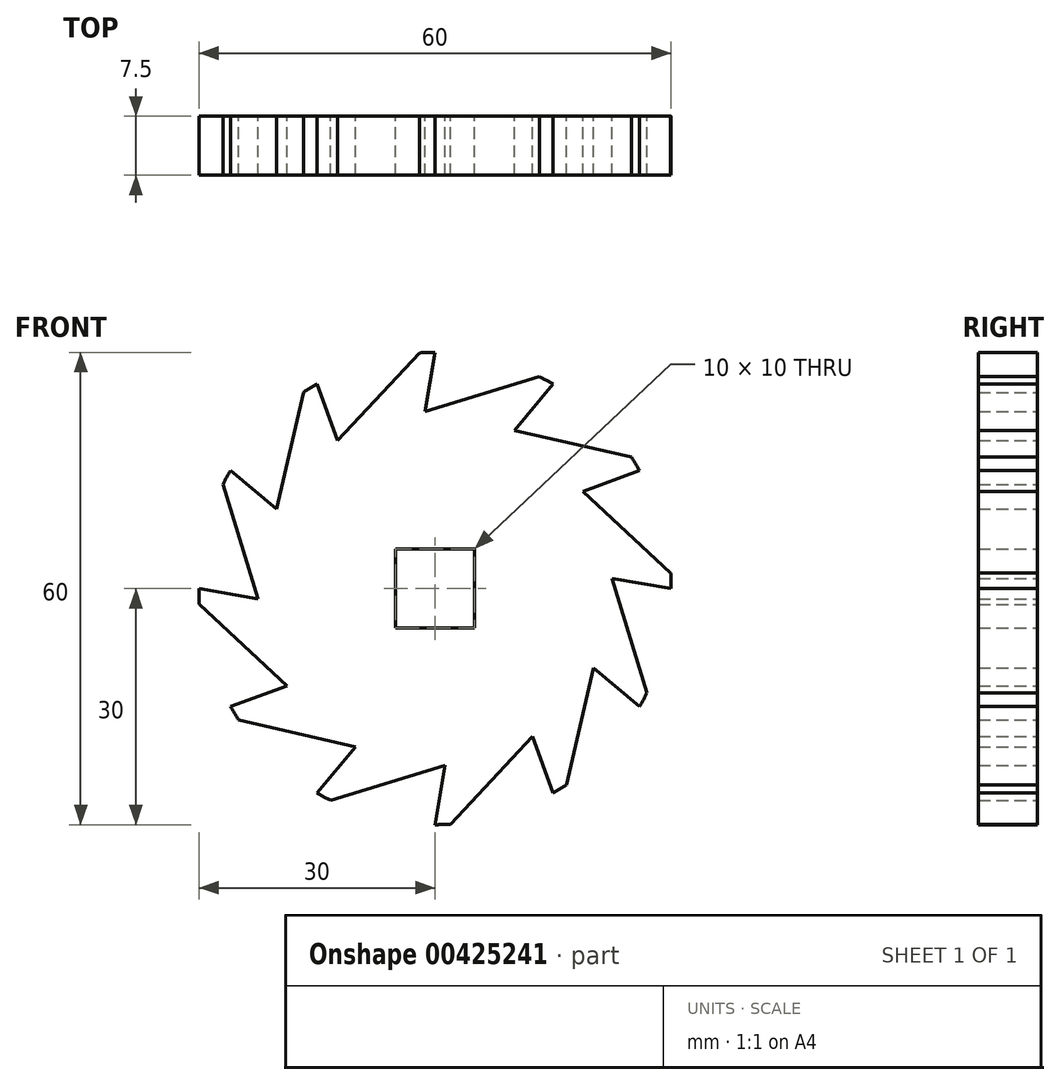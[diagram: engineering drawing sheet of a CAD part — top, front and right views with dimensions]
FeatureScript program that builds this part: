
annotation { "Feature Type Name" : "Feature", "Feature Type Description" : "" }
export const myFeature = defineFeature(function(context is Context, id is Id, definition is map)
    precondition{}
    {
        {
            var Q0;
            Q0=qCreatedBy(makeId("Front.planeOp"),FACE);
            var sketch = newSketch(context, id + "F0", { "sketchPlane" : qUnion([Q0])});
            skCircle(sketch, "E0", {"center": v(0, 0) * mm, "radius": 22.5 * mm, "construction": true});
            skLineSegment(sketch, "E1.bottom", {"start": v(5, 5) * mm, "end": v(-5, 5) * mm});
            skLineSegment(sketch, "E1.top", {"start": v(5, -5) * mm, "end": v(-5, -5) * mm});
            skLineSegment(sketch, "E1.left", {"start": v(5, 5) * mm, "end": v(5, -5) * mm});
            skLineSegment(sketch, "E1.right", {"start": v(-5, 5) * mm, "end": v(-5, -5) * mm});
            skCircle(sketch, "E2", {"center": v(0, 0) * mm, "radius": 30 * mm, "construction": true});
            skLineSegment(sketch, "E3", {"start": v(0, 0) * mm, "end": v(0, 30) * mm, "construction": true});
            skLineSegment(sketch, "E4", {"start": v(0, 0) * mm, "end": v(13.24, 26.92) * mm, "construction": true});
            skLineSegment(sketch, "E5", {"start": v(0, 30) * mm, "end": v(-1.3, 22.46) * mm, "construction": true});
            skLineSegment(sketch, "E6", {"start": v(-1.3, 22.46) * mm, "end": v(13.24, 26.92) * mm});
            skArc(sketch, "E7", {"start": v(13.24, 26.92) * mm, "mid": v(14.13, 26.46) * mm, "end": v(15, 25.98) * mm});
            skLineSegment(sketch, "E8", {"start": v(0, 0) * mm, "end": v(15, 25.98) * mm, "construction": true});
            skLineSegment(sketch, "E9.1.0", {"start": v(15, 25.98) * mm, "end": v(10.1, 20.1) * mm});
            skLineSegment(sketch, "E9.anchor1", {"start": v(0, 0) * mm, "end": v(-1.3, 22.46) * mm, "construction": true});
            skLineSegment(sketch, "E9.anchor2", {"start": v(0, 0) * mm, "end": v(10.1, 20.1) * mm, "construction": true});
            skLineSegment(sketch, "E10.1.0", {"start": v(-12.36, 18.8) * mm, "end": v(-2, 29.93) * mm});
            skArc(sketch, "E10.1.1", {"start": v(-2, 29.93) * mm, "mid": v(-1, 29.98) * mm, "end": v(0, 30) * mm});
            skLineSegment(sketch, "E10.1.2", {"start": v(0, 30) * mm, "end": v(-1.3, 22.46) * mm});
            skLineSegment(sketch, "E10.2.0", {"start": v(-20.1, 10.1) * mm, "end": v(-16.7, 24.93) * mm});
            skArc(sketch, "E10.2.1", {"start": v(-16.7, 24.93) * mm, "mid": v(-15.85, 25.47) * mm, "end": v(-15, 25.98) * mm});
            skLineSegment(sketch, "E10.2.2", {"start": v(-15, 25.98) * mm, "end": v(-12.36, 18.8) * mm});
            skLineSegment(sketch, "E10.3.0", {"start": v(-22.46, -1.3) * mm, "end": v(-26.92, 13.24) * mm});
            skArc(sketch, "E10.3.1", {"start": v(-26.92, 13.24) * mm, "mid": v(-26.46, 14.13) * mm, "end": v(-25.98, 15) * mm});
            skLineSegment(sketch, "E10.3.2", {"start": v(-25.98, 15) * mm, "end": v(-20.1, 10.1) * mm});
            skLineSegment(sketch, "E10.4.0", {"start": v(-18.8, -12.36) * mm, "end": v(-29.93, -2) * mm});
            skArc(sketch, "E10.4.1", {"start": v(-29.93, -2) * mm, "mid": v(-29.98, -1) * mm, "end": v(-30, 0) * mm});
            skLineSegment(sketch, "E10.4.2", {"start": v(-30, 0) * mm, "end": v(-22.46, -1.3) * mm});
            skLineSegment(sketch, "E10.5.0", {"start": v(-10.1, -20.1) * mm, "end": v(-24.93, -16.7) * mm});
            skArc(sketch, "E10.5.1", {"start": v(-24.93, -16.7) * mm, "mid": v(-25.47, -15.85) * mm, "end": v(-25.98, -15) * mm});
            skLineSegment(sketch, "E10.5.2", {"start": v(-25.98, -15) * mm, "end": v(-18.8, -12.36) * mm});
            skLineSegment(sketch, "E10.6.0", {"start": v(1.3, -22.46) * mm, "end": v(-13.24, -26.92) * mm});
            skArc(sketch, "E10.6.1", {"start": v(-13.24, -26.92) * mm, "mid": v(-14.13, -26.46) * mm, "end": v(-15, -25.98) * mm});
            skLineSegment(sketch, "E10.6.2", {"start": v(-15, -25.98) * mm, "end": v(-10.1, -20.1) * mm});
            skLineSegment(sketch, "E10.7.0", {"start": v(12.36, -18.8) * mm, "end": v(2, -29.93) * mm});
            skArc(sketch, "E10.7.1", {"start": v(2, -29.93) * mm, "mid": v(1, -29.98) * mm, "end": v(0, -30) * mm});
            skLineSegment(sketch, "E10.7.2", {"start": v(0, -30) * mm, "end": v(1.3, -22.46) * mm});
            skLineSegment(sketch, "E10.8.0", {"start": v(20.1, -10.1) * mm, "end": v(16.7, -24.93) * mm});
            skArc(sketch, "E10.8.1", {"start": v(16.7, -24.93) * mm, "mid": v(15.85, -25.47) * mm, "end": v(15, -25.98) * mm});
            skLineSegment(sketch, "E10.8.2", {"start": v(15, -25.98) * mm, "end": v(12.36, -18.8) * mm});
            skLineSegment(sketch, "E10.9.0", {"start": v(22.46, 1.3) * mm, "end": v(26.92, -13.24) * mm});
            skArc(sketch, "E10.9.1", {"start": v(26.92, -13.24) * mm, "mid": v(26.46, -14.13) * mm, "end": v(25.98, -15) * mm});
            skLineSegment(sketch, "E10.9.2", {"start": v(25.98, -15) * mm, "end": v(20.1, -10.1) * mm});
            skLineSegment(sketch, "E10.10.0", {"start": v(18.8, 12.36) * mm, "end": v(29.93, 2) * mm});
            skArc(sketch, "E10.10.1", {"start": v(29.93, 2) * mm, "mid": v(29.98, 1) * mm, "end": v(30, 0) * mm});
            skLineSegment(sketch, "E10.10.2", {"start": v(30, 0) * mm, "end": v(22.46, 1.3) * mm});
            skLineSegment(sketch, "E10.11.0", {"start": v(10.1, 20.1) * mm, "end": v(24.93, 16.7) * mm});
            skArc(sketch, "E10.11.1", {"start": v(24.93, 16.7) * mm, "mid": v(25.47, 15.85) * mm, "end": v(25.98, 15) * mm});
            skLineSegment(sketch, "E10.11.2", {"start": v(25.98, 15) * mm, "end": v(18.8, 12.36) * mm});
            skSolve(sketch);
        }
        {
            var Q0;
            Q0=makeQuery(id+"F0.imprint","IMPRINT",FACE,{"disambiguationData":[TD([[makeQuery(id+"F0.imprint","IMPRINT",EDGE,{"derivedFrom":sQuery(id+"F0.wireOp",EDGE,"E1.bottom")}),-1.0]])]});
            extrude(context, id + "F1", {"entities" : qUnion([Q0]), "endBound" : BoundingType.SYMMETRIC, "depth" : 7.5 * mm});
        }
    });
